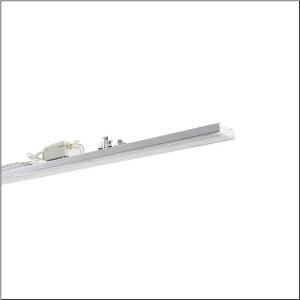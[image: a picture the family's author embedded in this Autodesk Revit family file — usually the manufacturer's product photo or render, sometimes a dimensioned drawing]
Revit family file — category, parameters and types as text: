
# Revit family: licross_r__21_recessed_mo_52te11dn4axg_b56d
name_source: partatom
category: Lighting Fixtures
units: mm (PartAtom-declared; Revit-internal decimal feet)

## family parameters
Cut with Voids When Loaded = No
Host = Face
Light Source = No
Part Type = Normal
Room Calculation Point = No
Round Connector Dimension = Use Diameter
Shared = No

## types (1)
- --- (1 x LED, 10120 lm, 58 W, 4000K)
    Apparent Load = 58 VA
    CIE Flux Codes = 89 96 99 100 100
    Color Rendering = 80
    Color Temperature = 4000K
    Default Elevation = 1800 mm
    Description = Licross® 21 Recessed MO, luminaire insert, of sheet steel, galvanised, coil coated, white, length: 1.500mm, width: 66mm, height: 67mm, LED rated luminous flux: 10.120lm, light colour: 840, control gear: DALI 2, with plug, 5-pole, with phase selection, mains connection: 220..240V, AC, 50/60Hz, rated input power: 58W, halogen-free wiring, primary light control with lens, of plastic, primary optical cover: cover, of PMMA, light emission: direct distribution, primary light characteristic: symmetric, protection rating (complete): IP54, insulation class (complete): insulation class I (protective earthing), certification: CE, ENEC, VDE, UKCA, protection symbol: D if used in an environment with non-conductive dust loads with corresponding accessories, impact resistance: IK06, permissible ambient temperature for indoor applications: -25..+35°C, corresponds to IFS (International Featured Standards) requirements for safety and quality in the food industry, reducing of maximum allowable ambient temperature of 5°C with ceiling mounting, LABS conformity tested according to VDMA 24364:2018-05, packaging unit: 1 piece
    Height = 58 mm
    Lamp = 1 x LED
    Lamp Light Flux = 10120 lm
    Lamp Power = 58 W
    Lamp count = 1
    Length = 1500 mm
    Luminous efficacy = 174 lm/W
    Manufacturer = Siteco
    ModVariant = No
    Model = 52TE11DN4AXG
    Mounting Place = Ceiling
    Mounting Type = Pendant
    Number of Poles = 1
    OnlyDefault = Yes
    Power Factor = 1
    Product Name = Licross® 21 Recessed MO
    Product group = luminaire insert
    ProductGroupID = 901
    Protection Class = Protection class I
    Protection Degree = IP 54
    RLX_Detail_Level = 1
    RLX_Emergency_Light_Flux = 0 lm
    RLX_Emergency_Type = 0
    RLX_Emergency_Type_DB = No
    RlxData = <blob elided: 24477 chars, md5=e074ae40>
    Socket = socket
    Standby Power = 0 W
    System Light Flux = 10120 lm
    System Power = 58 W
    Type Comments = factory setting: luminous flux: 100 % | dim-lin: 254 | 390 mA
    Type Image = l_1296930.jpg
    URL = http://relux.com
    VarID = @adj_058417
    Voltage = 0 V
    Weight = 0.00 kg
    Width = 66 mm

## geometry (parser evidence)
native form markers: Blend x4, Sweep x11
no freeform markers — native parametric forms only
